# Revit family: Cellular Beam
name_source: partatom
category: Structural Framing
revit_build: Autodesk Revit 2017 (Build: 20161117_1200(x64)
units: mm (PartAtom-declared; Revit-internal decimal feet)

## family parameters
Always export as geometry = No
Always vertical = Yes
Cut with Voids When Loaded = No
Material for Model Behavior = Steel
OmniClass Number = 23.25.30.11.14.14
OmniClass Title = Beams
Section Shape = Not Defined
Shared = No
Show family pre-cut in plan views = Yes
Structural Framing Length Roundoff = 1 mm

## types (2) — shared parameters
tf1 = 9 mm  [stored 0.0295276 ft]
tw1 = 6 mm  [stored 0.019685 ft]

## per-type parameters (varying)
| type | Do | Name1 | Name2 | S | W1 | W2 | bf1 | bf2 | d | d1 | d2 | dt1 | dt2 | e | h1 | h2 | k1 | k2 | r1 | r2 | tf2 | tw2 |
| LB460X28.3 | 300 mm  [stored 0.984252 ft] | W310X28.3 | W310X28.3 | 450 mm  [stored 1.47638 ft] | 28.3 | 28.3 | 102 mm | 102 mm | 459 mm  [stored 1.50591 ft] | 309 mm  [stored 1.01378 ft] | 309 mm  [stored 1.01378 ft] | 80 mm | 80 mm | 150 mm | 150 mm | 150 mm | 22 mm  [stored 0.0721785 ft] | 22 mm  [stored 0.0721785 ft] | 13 mm | 13 mm | 9 mm  [stored 0.0295276 ft] | 6 mm  [stored 0.019685 ft] |
| LB530X32.9/39 | 360 mm  [stored 1.1811 ft] | W360X32.9 | W360X39 | 520 mm  [stored 1.70604 ft] | 32.9 | 39 | 127 mm | 128 mm  [stored 0.419948 ft] | 531 mm  [stored 1.74213 ft] | 349 mm  [stored 1.14501 ft] | 353 mm  [stored 1.15814 ft] | 85 mm | 87 mm | 160 mm | 180 mm  [stored 0.590551 ft] | 180 mm  [stored 0.590551 ft] | 26 mm | 28 mm  [stored 0.0918635 ft] | 18 mm | 17 mm | 11 mm | 7 mm  [stored 0.0229659 ft] |

note: [stored X ft] marks values corroborated as IEEE doubles in the binary element streams (Revit-internal decimal feet)

## geometry (parser evidence)
native form markers: Blend x4, Sweep x4
no freeform markers — native parametric forms only
